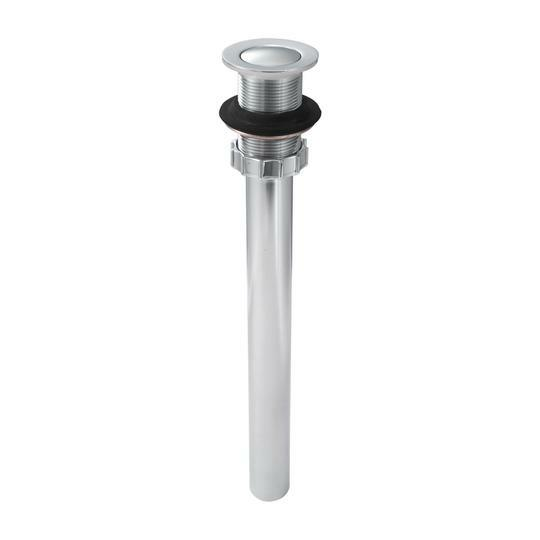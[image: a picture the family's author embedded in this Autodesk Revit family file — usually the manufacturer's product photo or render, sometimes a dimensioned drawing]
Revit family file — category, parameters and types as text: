
# Revit family: 01-2906-11 DESAGUE LARGO PUSH METAL SIN REBOSE
name_source: partatom
category: Aparatos sanitarios
revit_build: Autodesk Revit 2018 (Build: 20170223_1515(x64)
units: mm (PartAtom-declared; Revit-internal decimal feet)

## family parameters
Anfitrión = Cara
Compartido = No
Corte con vacíos al cargar = No
Cota de conector redondo = Diámetro de uso
Número OmniClass = 23.31.11.00
Punto de cálculo de habitación = No
Tipo de pieza = Normal

## types (1)
- 01-2906-11
    Acople = 31.8 mm  [stored 0.104331 ft]
    Alto = 377 mm  [stored 1.23688 ft]
    Caucho = Caucho
    Conexión AC = Sí
    Conexión AF = Sí
    Conexión de residuos = No
    Conexión de ventilación = No
    Descripción = Desague
    Diametro = 61 mm
    Elevación por defecto = 0 mm  [stored 0 ft]
    Fabricante = Gricol
    Imagen de tipo = DESAGUE LARGO PUSH METAL SIN REBOSE.jpg
    Link Ficha Tecnica = http://infotecnica.gricol.com
    Metal  Laton cromado = Metal Laton Cromado
    Modelo = 01-2906-11
    Plastico ABS Cromado = Plastico - ABS Cromado
    Product Name = DESAGUE LARGO PUSH METAL SIN REBOSE
    URL = https://www.gricol.com

note: [stored X ft] marks values corroborated as IEEE doubles in the binary element streams (Revit-internal decimal feet)

## geometry (parser evidence)
native form markers: Blend x2, Sweep x5
no freeform markers — native parametric forms only
